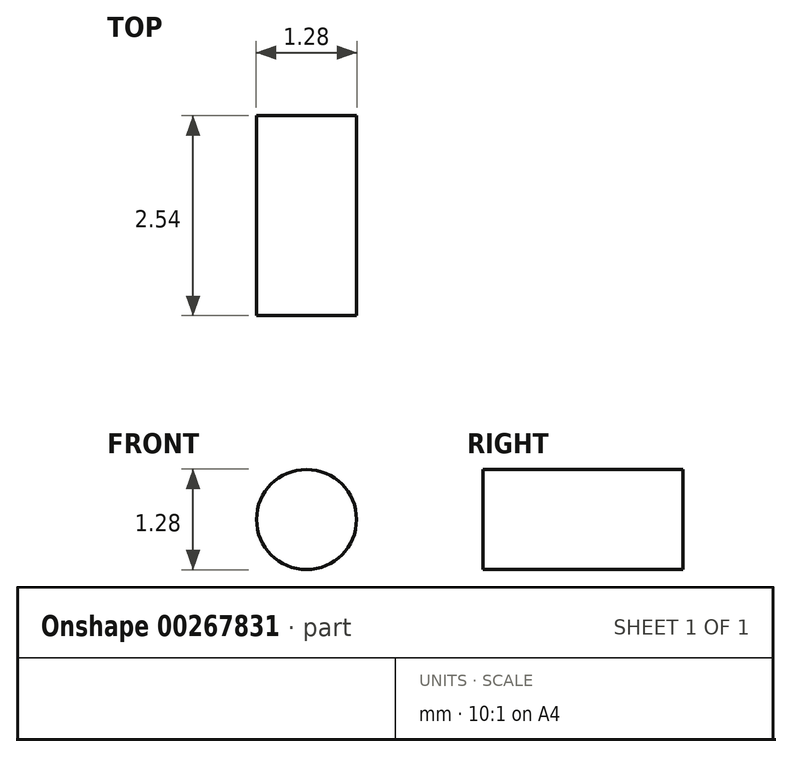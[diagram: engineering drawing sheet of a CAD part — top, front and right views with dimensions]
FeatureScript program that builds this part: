
annotation { "Feature Type Name" : "Feature", "Feature Type Description" : "" }
export const myFeature = defineFeature(function(context is Context, id is Id, definition is map)
    precondition{}
    {
        {
            var Q0;
            Q0=qCreatedBy(makeId("Front.planeOp"),FACE);
            var sketch = newSketch(context, id + "F0", { "sketchPlane" : qUnion([Q0])});
            skCircle(sketch, "E0", {"center": v(0, 0) * mm, "radius": 0.64 * mm});
            skSolve(sketch);
        }
        {
            var Q0;
            Q0=makeQuery(id+"F0.imprint","IMPRINT",FACE,{"disambiguationData":[TD([[makeQuery(id+"F0.imprint","IMPRINT",EDGE,{"derivedFrom":sQuery(id+"F0.wireOp",EDGE,"E0")}),1.0]])]});
            extrude(context, id + "F1", {"entities" : qUnion([Q0]), "depth" : 2.54 * mm});
        }
    });
